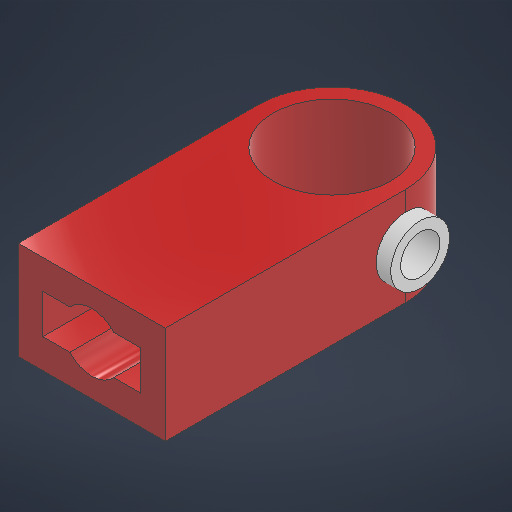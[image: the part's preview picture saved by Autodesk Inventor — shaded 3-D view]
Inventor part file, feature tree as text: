
AUTODESK INVENTOR PART (.ipt)
format: ipt  version: 2025.1 (Build 291241000, 241)  size: 299,520 bytes
history: native  units: in
note: dims shown in document units (in); Inventor stores cm internally (conversion verified against a paired STEP export)
features: sketch x5, extrude x4, other x1
ambient origin geometry x8: Origin, YZ Plane, XZ Plane, XY Plane, X Axis, Y Axis, Z Axis, Center Point
bodies: Solid1 (feature_tree)
feature tree (10):
  extrude  "Extrusion1"  Depth=0.1969in TaperAngle=0.0deg
  extrude  "Extrusion2"  Depth=0.1969in
  sketch  "Sketch3"  dims[d10=0.0787in d11=0.3346in d12=0.0in]
  extrude  "Extrusion3"  Depth=0.3346in TaperAngle=0.0deg
  extrude  "Extrusion4"  Depth=0.1181in
  sketch  "Sketch1"  dims[d0=0.315in d1=0.2362in d2=0.315in d3=0.1969in d4=0.2953in d5=0.2953in d6=0.1969in d7=0.0in]
  sketch  "Sketch2"  dims[d8=0.1181in d9=0.1969in]
  sketch  "Sketch4"  dims[d13=0.3346in d14=0.1181in]
  sketch  "Sketch5"  dims[d15=0.0591in d16=0.0in d17=0.0787in d18=0.1216in d19=0.0in]
  other  "Finish1"
